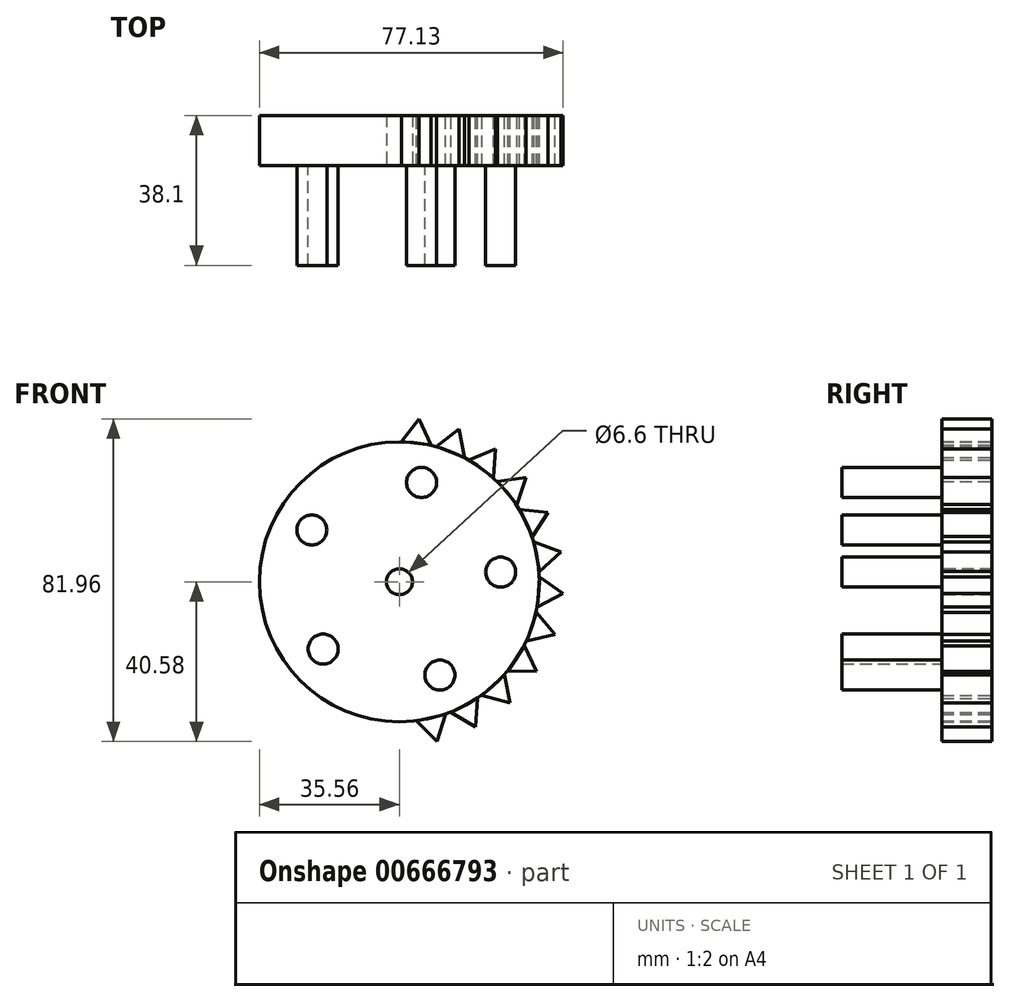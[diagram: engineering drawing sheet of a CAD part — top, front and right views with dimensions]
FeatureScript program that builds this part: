
annotation { "Feature Type Name" : "Feature", "Feature Type Description" : "" }
export const myFeature = defineFeature(function(context is Context, id is Id, definition is map)
    precondition{}
    {
        {
            var Q0;
            Q0=qCreatedBy(makeId("Front.planeOp"),FACE);
            var sketch = newSketch(context, id + "F0", { "sketchPlane" : qUnion([Q0])});
            skCircle(sketch, "E0", {"center": v(0, 0) * mm, "radius": 35.56 * mm});
            skSolve(sketch);
        }
        {
            var Q0;
            Q0=makeQuery(id+"F0.imprint","IMPRINT",FACE,{"disambiguationData":[TD([[makeQuery(id+"F0.imprint","IMPRINT",EDGE,{"derivedFrom":sQuery(id+"F0.wireOp",EDGE,"E0")}),1.0]])]});
            var sketch = newSketch(context, id + "F1", { "sketchPlane" : qUnion([Q0])});
            skLineSegment(sketch, "E1", {"start": v(-35.34, 0) * mm, "end": v(35.19, 0) * mm});
            skSolve(sketch);
        }
        {
            var Q0;
            Q0=qCreatedBy(makeId("Front.planeOp"),FACE);
            var sketch = newSketch(context, id + "F2", { "sketchPlane" : qUnion([Q0])});
            skLineSegment(sketch, "E2", {"start": v(0.47, 35.64) * mm, "end": v(4.95, 41.38) * mm});
            skLineSegment(sketch, "E3", {"start": v(4.95, 41.38) * mm, "end": v(8.04, 34.77) * mm});
            skLineSegment(sketch, "E4", {"start": v(8.04, 34.77) * mm, "end": v(0.47, 35.64) * mm});
            skLineSegment(sketch, "E5", {"start": v(8.04, 34.77) * mm, "end": v(9.25, 34.4) * mm});
            skLineSegment(sketch, "E6.1.0", {"start": v(9.4, 34.38) * mm, "end": v(15.19, 38.81) * mm});
            skLineSegment(sketch, "E6.1.1", {"start": v(15.19, 38.81) * mm, "end": v(16.5, 31.63) * mm});
            skLineSegment(sketch, "E6.1.2", {"start": v(16.5, 31.63) * mm, "end": v(9.4, 34.38) * mm});
            skLineSegment(sketch, "E6.1.3", {"start": v(16.5, 31.63) * mm, "end": v(17.6, 30.97) * mm});
            skLineSegment(sketch, "E6.2.0", {"start": v(17.74, 30.92) * mm, "end": v(24.45, 33.75) * mm});
            skLineSegment(sketch, "E6.2.1", {"start": v(24.45, 33.75) * mm, "end": v(23.92, 26.47) * mm});
            skLineSegment(sketch, "E6.2.2", {"start": v(23.92, 26.47) * mm, "end": v(17.74, 30.92) * mm});
            skLineSegment(sketch, "E6.2.3", {"start": v(23.92, 26.47) * mm, "end": v(24.8, 25.56) * mm});
            skLineSegment(sketch, "E6.3.0", {"start": v(24.93, 25.47) * mm, "end": v(32.14, 26.53) * mm});
            skLineSegment(sketch, "E6.3.1", {"start": v(32.14, 26.53) * mm, "end": v(29.8, 19.62) * mm});
            skLineSegment(sketch, "E6.3.2", {"start": v(29.8, 19.62) * mm, "end": v(24.93, 25.47) * mm});
            skLineSegment(sketch, "E6.3.3", {"start": v(29.8, 19.62) * mm, "end": v(30.43, 18.51) * mm});
            skLineSegment(sketch, "E6.4.0", {"start": v(30.53, 18.4) * mm, "end": v(37.77, 17.6) * mm});
            skLineSegment(sketch, "E6.4.1", {"start": v(37.77, 17.6) * mm, "end": v(33.78, 11.5) * mm});
            skLineSegment(sketch, "E6.4.2", {"start": v(33.78, 11.5) * mm, "end": v(30.53, 18.4) * mm});
            skLineSegment(sketch, "E6.4.3", {"start": v(33.78, 11.5) * mm, "end": v(34.1, 10.27) * mm});
            skLineSegment(sketch, "E6.5.0", {"start": v(34.17, 10.14) * mm, "end": v(40.99, 7.56) * mm});
            skLineSegment(sketch, "E6.5.1", {"start": v(40.99, 7.56) * mm, "end": v(35.58, 2.65) * mm});
            skLineSegment(sketch, "E6.5.2", {"start": v(35.58, 2.65) * mm, "end": v(34.17, 10.14) * mm});
            skLineSegment(sketch, "E6.5.3", {"start": v(35.58, 2.65) * mm, "end": v(35.6, 1.38) * mm});
            skLineSegment(sketch, "E6.6.0", {"start": v(35.62, 1.23) * mm, "end": v(41.57, -2.98) * mm});
            skLineSegment(sketch, "E6.6.1", {"start": v(41.57, -2.98) * mm, "end": v(35.1, -6.37) * mm});
            skLineSegment(sketch, "E6.6.2", {"start": v(35.1, -6.37) * mm, "end": v(35.62, 1.23) * mm});
            skLineSegment(sketch, "E6.6.3", {"start": v(35.1, -6.37) * mm, "end": v(34.8, -7.6) * mm});
            skLineSegment(sketch, "E6.7.0", {"start": v(34.8, -7.76) * mm, "end": v(39.5, -13.32) * mm});
            skLineSegment(sketch, "E6.7.1", {"start": v(39.5, -13.32) * mm, "end": v(32.38, -14.99) * mm});
            skLineSegment(sketch, "E6.7.2", {"start": v(32.38, -14.99) * mm, "end": v(34.8, -7.76) * mm});
            skLineSegment(sketch, "E6.7.3", {"start": v(32.38, -14.99) * mm, "end": v(31.77, -16.1) * mm});
            skLineSegment(sketch, "E6.8.0", {"start": v(31.73, -16.25) * mm, "end": v(34.88, -22.81) * mm});
            skLineSegment(sketch, "E6.8.1", {"start": v(34.88, -22.81) * mm, "end": v(27.58, -22.64) * mm});
            skLineSegment(sketch, "E6.8.2", {"start": v(27.58, -22.64) * mm, "end": v(31.73, -16.25) * mm});
            skLineSegment(sketch, "E6.8.3", {"start": v(27.58, -22.64) * mm, "end": v(26.71, -23.57) * mm});
            skLineSegment(sketch, "E6.9.0", {"start": v(26.63, -23.7) * mm, "end": v(28.03, -30.84) * mm});
            skLineSegment(sketch, "E6.9.1", {"start": v(28.03, -30.84) * mm, "end": v(21.01, -28.84) * mm});
            skLineSegment(sketch, "E6.9.2", {"start": v(21.01, -28.84) * mm, "end": v(26.63, -23.7) * mm});
            skLineSegment(sketch, "E6.9.3", {"start": v(21.01, -28.84) * mm, "end": v(19.94, -29.52) * mm});
            skPoint(sketch, "E6.center", {"position": v(0, 0) * mm});
            skLineSegment(sketch, "E6.anchor1", {"start": v(0, 0) * mm, "end": v(0.47, 35.64) * mm, "construction": true});
            skLineSegment(sketch, "E6.anchor2", {"start": v(0, 0) * mm, "end": v(11.75, -33.65) * mm, "construction": true});
            skLineSegment(sketch, "E7.1.10.0", {"start": v(19.83, -29.62) * mm, "end": v(19.39, -36.9) * mm});
            skLineSegment(sketch, "E7.3.10.0", {"start": v(19.39, -36.9) * mm, "end": v(13.1, -33.2) * mm});
            skLineSegment(sketch, "E7.6.10.0", {"start": v(13.1, -33.2) * mm, "end": v(19.83, -29.62) * mm});
            skLineSegment(sketch, "E7.9.10.0", {"start": v(13.1, -33.2) * mm, "end": v(11.88, -33.58) * mm});
            skLineSegment(sketch, "E7.1.11.0", {"start": v(11.75, -33.65) * mm, "end": v(9.5, -40.58) * mm});
            skLineSegment(sketch, "E7.3.11.0", {"start": v(9.5, -40.58) * mm, "end": v(4.34, -35.42) * mm});
            skLineSegment(sketch, "E7.6.11.0", {"start": v(4.34, -35.42) * mm, "end": v(11.75, -33.65) * mm});
            skLineSegment(sketch, "E7.9.11.0", {"start": v(4.34, -35.42) * mm, "end": v(3.07, -35.49) * mm});
            skSolve(sketch);
        }
        {
            var Q0;
            Q0=makeQuery(id+"F1.imprint","IMPRINT",FACE,{"disambiguationData":[TD([[makeQuery(id+"F1.imprint","IMPRINT",EDGE,{"derivedFrom":makeQuery(id+"F0.imprint","IMPRINT",EDGE,{"derivedFrom":sQuery(id+"F0.wireOp",EDGE,"E0")})}),1.0]])]});
            var sketch = newSketch(context, id + "F3", { "sketchPlane" : qUnion([Q0])});
            skCircle(sketch, "E8", {"center": v(5.62, 25.23) * mm, "radius": 3.81 * mm});
            skCircle(sketch, "E9.1.0", {"center": v(-22.26, 13.15) * mm, "radius": 3.81 * mm});
            skCircle(sketch, "E9.2.0", {"center": v(-19.38, -17.1) * mm, "radius": 3.81 * mm});
            skCircle(sketch, "E9.3.0", {"center": v(10.28, -23.72) * mm, "radius": 3.81 * mm});
            skCircle(sketch, "E9.4.0", {"center": v(25.73, 2.45) * mm, "radius": 3.81 * mm});
            skPoint(sketch, "E9.center", {"position": v(0, 0) * mm});
            skLineSegment(sketch, "E10", {"start": v(-30.47, 18.28) * mm, "end": v(-25.49, 15.17) * mm});
            skSolve(sketch);
        }
        {
            var Q0;
            Q0=makeQuery(id+"F0.imprint","IMPRINT",FACE,{"disambiguationData":[TD([[makeQuery(id+"F0.imprint","IMPRINT",EDGE,{"derivedFrom":sQuery(id+"F0.wireOp",EDGE,"E0")}),1.0]])]});
            var sketch = newSketch(context, id + "F4", { "sketchPlane" : qUnion([Q0])});
            skSolve(sketch);
        }
        {
            var Q0;
            Q0 = qSketchRegion(id + "F4", true);
            var Q1;
            Q1=makeQuery(id+"F0.imprint","IMPRINT",FACE,{"disambiguationData":[TD([[makeQuery(id+"F0.imprint","IMPRINT",EDGE,{"derivedFrom":sQuery(id+"F0.wireOp",EDGE,"E0")}),1.0]])]});
            var Q2;
            Q2=makeQuery(id+"F2.imprint","IMPRINT",FACE,{"disambiguationData":[TD([[makeQuery(id+"F2.imprint","IMPRINT",EDGE,{"derivedFrom":sQuery(id+"F2.wireOp",EDGE,"E2")}),-1.0]])]});
            var Q3;
            Q3=makeQuery(id+"F2.imprint","IMPRINT",FACE,{"disambiguationData":[TD([[makeQuery(id+"F2.imprint","IMPRINT",EDGE,{"derivedFrom":sQuery(id+"F2.wireOp",EDGE,"E6.1.0")}),-1.0]])]});
            var Q4;
            Q4=makeQuery(id+"F2.imprint","IMPRINT",FACE,{"disambiguationData":[TD([[makeQuery(id+"F2.imprint","IMPRINT",EDGE,{"derivedFrom":sQuery(id+"F2.wireOp",EDGE,"E6.2.0")}),-1.0]])]});
            var Q5;
            Q5=makeQuery(id+"F2.imprint","IMPRINT",FACE,{"disambiguationData":[TD([[makeQuery(id+"F2.imprint","IMPRINT",EDGE,{"derivedFrom":sQuery(id+"F2.wireOp",EDGE,"E6.3.0")}),-1.0]])]});
            var Q6;
            Q6=makeQuery(id+"F2.imprint","IMPRINT",FACE,{"disambiguationData":[TD([[makeQuery(id+"F2.imprint","IMPRINT",EDGE,{"derivedFrom":sQuery(id+"F2.wireOp",EDGE,"E6.4.0")}),-1.0]])]});
            var Q7;
            Q7=makeQuery(id+"F2.imprint","IMPRINT",FACE,{"disambiguationData":[TD([[makeQuery(id+"F2.imprint","IMPRINT",EDGE,{"derivedFrom":sQuery(id+"F2.wireOp",EDGE,"E6.5.0")}),-1.0]])]});
            var Q8;
            Q8=makeQuery(id+"F2.imprint","IMPRINT",FACE,{"disambiguationData":[TD([[makeQuery(id+"F2.imprint","IMPRINT",EDGE,{"derivedFrom":sQuery(id+"F2.wireOp",EDGE,"E6.6.0")}),-1.0]])]});
            var Q9;
            Q9=makeQuery(id+"F2.imprint","IMPRINT",FACE,{"disambiguationData":[TD([[makeQuery(id+"F2.imprint","IMPRINT",EDGE,{"derivedFrom":sQuery(id+"F2.wireOp",EDGE,"E6.7.0")}),-1.0]])]});
            var Q10;
            Q10=makeQuery(id+"F2.imprint","IMPRINT",FACE,{"disambiguationData":[TD([[makeQuery(id+"F2.imprint","IMPRINT",EDGE,{"derivedFrom":sQuery(id+"F2.wireOp",EDGE,"E6.8.0")}),-1.0]])]});
            var Q11;
            Q11=makeQuery(id+"F2.imprint","IMPRINT",FACE,{"disambiguationData":[TD([[makeQuery(id+"F2.imprint","IMPRINT",EDGE,{"derivedFrom":sQuery(id+"F2.wireOp",EDGE,"E6.9.0")}),-1.0]])]});
            var Q12;
            Q12=makeQuery(id+"F2.imprint","IMPRINT",FACE,{"disambiguationData":[TD([[makeQuery(id+"F2.imprint","IMPRINT",EDGE,{"derivedFrom":sQuery(id+"F2.wireOp",EDGE,"E7.1.10.0")}),-1.0]])]});
            var Q13;
            Q13=makeQuery(id+"F2.imprint","IMPRINT",FACE,{"disambiguationData":[TD([[makeQuery(id+"F2.imprint","IMPRINT",EDGE,{"derivedFrom":sQuery(id+"F2.wireOp",EDGE,"E7.1.11.0")}),-1.0]])]});
            extrude(context, id + "F5", {"entities" : qUnion([Q0, Q1, Q2, Q3, Q4, Q5, Q6, Q7, Q8, Q9, Q10, Q11, Q12, Q13]), "depth" : 12.7 * mm, "offsetDistance" : 25.4 * mm});
        }
        {
            var Q0;
            Q0 = qSketchRegion(id + "F3", true);
            extrude(context, id + "F6", {"entities" : qUnion([Q0]), "operationType" : NewBodyOperationType.ADD, "depth" : 38.1 * mm, "offsetDistance" : 25.4 * mm});
        }
        {
            var Q0;
            Q0=makeQuery(id+"F5.opExtrude","CAP_FACE",FACE,{"disambiguationData":[OSD([sQuery(id+"F0.wireOp",EDGE,"E0")])],"isStart":false});
            var sketch = newSketch(context, id + "F7", { "sketchPlane" : qUnion([Q0])});
            skCircle(sketch, "E11", {"center": v(0, 0) * mm, "radius": 3.3 * mm});
            skSolve(sketch);
        }
        {
            var Q0;
            Q0 = qSketchRegion(id + "F7", true);
            extrude(context, id + "F8", {"entities" : qUnion([Q0]), "operationType" : NewBodyOperationType.REMOVE, "oppositeDirection" : true, "depth" : 25.4 * mm, "offsetDistance" : 25.4 * mm});
        }
    });
